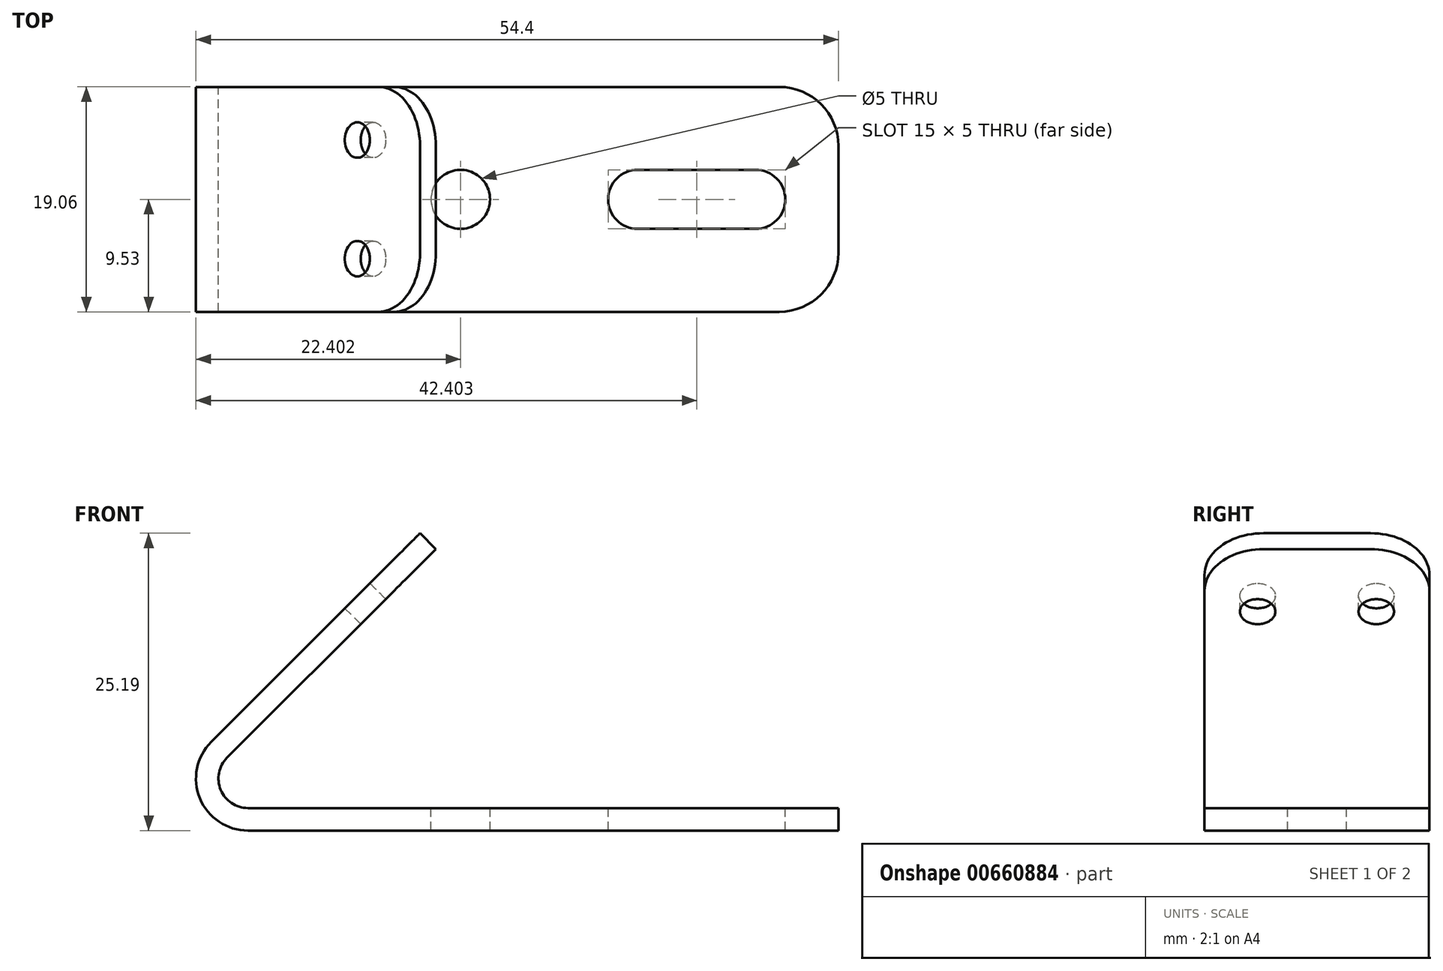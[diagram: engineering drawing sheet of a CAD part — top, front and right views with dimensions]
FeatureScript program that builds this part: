
annotation { "Feature Type Name" : "Feature", "Feature Type Description" : "" }
export const myFeature = defineFeature(function(context is Context, id is Id, definition is map)
    precondition{}
    {
        {
            var Q0;
            Q0=qCreatedBy(makeId("Front.planeOp"),FACE);
            var sketch = newSketch(context, id + "F0", { "sketchPlane" : qUnion([Q0])});
            skLineSegment(sketch, "E0", {"start": v(10.62, 0) * mm, "end": v(60.62, 0) * mm});
            skLineSegment(sketch, "E1", {"start": v(60.62, 0) * mm, "end": v(60.62, 1.9) * mm});
            skLineSegment(sketch, "E2", {"start": v(60.62, 1.9) * mm, "end": v(0, 1.9) * mm});
            skLineSegment(sketch, "E3", {"start": v(7.51, 7.51) * mm, "end": v(25.19, 25.19) * mm});
            skPoint(sketch, "E4.visualSharp", {"position": v(0, 0) * mm});
            skArc(sketch, "E4.filletArc", {"start": v(7.51, 7.51) * mm, "mid": v(6.56, 2.72) * mm, "end": v(10.62, 0) * mm});
            skLineSegment(sketch, "E5", {"start": v(25.19, 25.19) * mm, "end": v(26.53, 23.85) * mm});
            skLineSegment(sketch, "E6", {"start": v(26.53, 23.85) * mm, "end": v(8.85, 6.17) * mm});
            skArc(sketch, "E7", {"start": v(8.85, 6.17) * mm, "mid": v(8.31, 3.44) * mm, "end": v(10.62, 1.9) * mm});
            skSolve(sketch);
        }
        {
            var Q0;
            Q0=qSketchRegion(id+"F0",true);
            extrude(context, id + "F1", {"entities" : qUnion([Q0]), "endBound" : BoundingType.SYMMETRIC, "depth" : 19.05 * mm});
        }
        {
            var Q0;
            Q0=makeQuery(id+"F1.opExtrude","SWEPT_FACE",FACE,{"disambiguationData":[OSD([sQuery(id+"F0.wireOp",EDGE,"E2")])]});
            var sketch = newSketch(context, id + "F2", { "sketchPlane" : qUnion([Q0])});
            skLineSegment(sketch, "E8.0", {"start": v(60.62, -9.53) * mm, "end": v(60.62, 9.52) * mm});
            skLineSegment(sketch, "E9.0", {"start": v(60.62, 9.53) * mm, "end": v(10.62, 9.53) * mm});
            skLineSegment(sketch, "E10.0", {"start": v(60.62, -9.53) * mm, "end": v(10.62, -9.53) * mm});
            skLineSegment(sketch, "E11", {"start": v(60.62, 0) * mm, "end": v(56.12, 0) * mm});
            skLineSegment(sketch, "E12", {"start": v(56.12, 0) * mm, "end": v(41.12, 0) * mm});
            skLineSegment(sketch, "E13", {"start": v(56.12, 0) * mm, "end": v(56.12, 2.5) * mm});
            skCircle(sketch, "E14", {"center": v(53.62, 0) * mm, "radius": 2.5 * mm});
            skCircle(sketch, "E15", {"center": v(43.62, 0) * mm, "radius": 2.5 * mm});
            skLineSegment(sketch, "E16", {"start": v(43.62, 2.5) * mm, "end": v(53.62, 2.5) * mm});
            skLineSegment(sketch, "E17", {"start": v(43.62, -2.5) * mm, "end": v(53.62, -2.5) * mm});
            skCircle(sketch, "E18", {"center": v(28.62, 0) * mm, "radius": 2.5 * mm});
            skSolve(sketch);
        }
        {
            var Q0;
            Q0=qSketchRegion(id+"F2",true);
            extrude(context, id + "F3", {"entities" : qUnion([Q0]), "operationType" : NewBodyOperationType.REMOVE, "endBound" : BoundingType.THROUGH_ALL, "oppositeDirection" : true, "depth" : 25 * mm});
        }
        {
            var Q0;
            Q0=makeQuery(id+"F1.opExtrude","SWEPT_FACE",FACE,{"disambiguationData":[OSD([sQuery(id+"F0.wireOp",EDGE,"E3")])]});
            var sketch = newSketch(context, id + "F4", { "sketchPlane" : qUnion([Q0])});
            skLineSegment(sketch, "E19.0", {"start": v(9.53, 35.62) * mm, "end": v(-9.52, 35.62) * mm});
            skLineSegment(sketch, "E19.1", {"start": v(9.53, 10.62) * mm, "end": v(-9.52, 10.62) * mm});
            skLineSegment(sketch, "E19.2", {"start": v(-9.53, 10.62) * mm, "end": v(-9.53, 35.62) * mm});
            skLineSegment(sketch, "E19.3", {"start": v(9.53, 10.62) * mm, "end": v(9.53, 35.62) * mm});
            skLineSegment(sketch, "E20", {"start": v(-9.53, 35.62) * mm, "end": v(-9.53, 28.12) * mm});
            skCircle(sketch, "E21", {"center": v(-5.03, 28.12) * mm, "radius": 1.5 * mm});
            skLineSegment(sketch, "E22", {"start": v(9.53, 6.22) * mm, "end": v(-9.52, 6.22) * mm});
            skCircle(sketch, "E23", {"center": v(5.03, 28.12) * mm, "radius": 1.5 * mm});
            skSolve(sketch);
        }
        {
            var Q0;
            Q0=makeQuery(id+"F4.imprint","IMPRINT",FACE,{"disambiguationData":[TD([[makeQuery(id+"F4.imprint","IMPRINT",EDGE,{"derivedFrom":sQuery(id+"F4.wireOp",EDGE,"E21")}),1.0]])]});
            var Q1;
            Q1=makeQuery(id+"F4.imprint","IMPRINT",FACE,{"disambiguationData":[TD([[makeQuery(id+"F4.imprint","IMPRINT",EDGE,{"derivedFrom":sQuery(id+"F4.wireOp",EDGE,"E23")}),1.0]])]});
            extrude(context, id + "F5", {"entities" : qUnion([Q0, Q1]), "operationType" : NewBodyOperationType.REMOVE, "endBound" : BoundingType.UP_TO_NEXT, "oppositeDirection" : true, "depth" : 25 * mm, "offsetDistance" : 25 * mm});
        }
        {
            var Q0;
            Q0=makeQuery(id+"F1.opExtrude","CAP_EDGE",EDGE,{"disambiguationData":[OSD([sQuery(id+"F0.wireOp",EDGE,"E5")])],"isStart":true});
            var Q1;
            Q1=makeQuery(id+"F1.opExtrude","CAP_EDGE",EDGE,{"disambiguationData":[OSD([sQuery(id+"F0.wireOp",EDGE,"E5")])],"isStart":false});
            var Q2;
            Q2=makeQuery(id+"F1.opExtrude","CAP_EDGE",EDGE,{"disambiguationData":[OSD([sQuery(id+"F0.wireOp",EDGE,"E1")])],"isStart":false});
            var Q3;
            Q3=makeQuery(id+"F1.opExtrude","CAP_EDGE",EDGE,{"disambiguationData":[OSD([sQuery(id+"F0.wireOp",EDGE,"E1")])],"isStart":true});
            fillet(context, id + "F6", {"entities" : qUnion([Q0, Q1, Q2, Q3]), "radius" : 5 * mm, "tangentPropagation" : true, "allowEdgeOverflow" : false});
        }
    });
